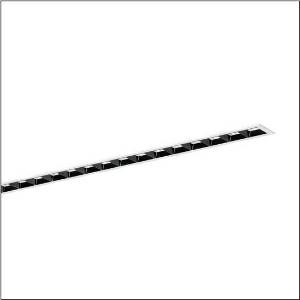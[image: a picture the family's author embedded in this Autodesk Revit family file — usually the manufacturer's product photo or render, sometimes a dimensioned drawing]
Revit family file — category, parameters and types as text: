
# Revit family: silica_21_51mx14tbt5w
name_source: partatom
category: Lighting Fixtures
units: mm (PartAtom-declared; Revit-internal decimal feet)

## family parameters
Cut with Voids When Loaded = No
Host = Face
Light Source = No
Part Type = Normal
Room Calculation Point = No
Round Connector Dimension = Use Diameter
Shared = No

## types (1)
- --- (1 x LED, 4100 lm, 40.5 W, 6500K)
    Apparent Load = 41 VA
    CIE Flux Codes = 74 94 99 100 100
    Color Rendering = 80
    Color Temperature = 6500K
    Default Elevation = 1800 mm
    Description = Silica 21, office luminaire, primary light control with darklight reflector, of PMMA, black, light emission: direct distribution, primary light characteristic: asymmetric, installation type: recessed, LED, rated luminous flux: 4.100lm, luminous efficacy: 96lm/W, light colour: 8tw, colour temperature: 2700..6500K, control gear: DALI DT8, with terminal, 3+2-pole, max. 2.5mm², mains connection: 220..240V, AC, 50/60Hz, rated input power: 42.6W, luminaire housing, of aluminium, traffic white (RAL 9016), length: 1.528mm, width: 79mm, height: 53mm, protection rating (complete): IP20, insulation class (complete): insulation class I (protective earthing), certification: CE, ENEC, VDE, permissible operating ambient temperature: 0..+35°C, standard: EN 50419, packaging unit: 1 piece
    Height = 0 mm  [stored 0 ft]
    Lamp = 1 x LED
    Lamp Light Flux = 4100 lm
    Lamp Power = 40.5 W
    Lamp count = 1
    Length = 1527 mm
    Luminous efficacy = 101 lm/W
    Manufacturer = Siteco
    ModVariant = No
    Model = 51MX14TBT5W
    Mounting Place = Ceiling
    Mounting Type = Recessed
    Number of Poles = 1
    OnlyDefault = Yes
    Power Factor = 1
    Product Name = Silica 21
    Product group = office luminaire | ceiling recessed
    ProductGroupID = 400
    Protection Class = Protection class I
    Protection Degree = IP 20
    RLX_Detail_Level = 1
    RLX_Emergency_Light_Flux = 0 lm
    RLX_Emergency_Type = 0
    RLX_Emergency_Type_DB = No
    RlxData = <blob elided: 39457 chars, md5=2ac0eb40>
    Socket = socket
    Standby Power = 0 W
    System Light Flux = 4100 lm
    System Power = 41 W
    Type Comments = individual setting
    Type Image = l_1335880.jpg
    URL = http://relux.com
    VarID = @adj_139523
    Voltage = 0 V
    Weight = 0.00 kg
    Width = 79 mm

note: [stored X ft] marks values corroborated as IEEE doubles in the binary element streams (Revit-internal decimal feet)

## geometry (parser evidence)
native form markers: Blend x4, Sweep x10
no freeform markers — native parametric forms only
